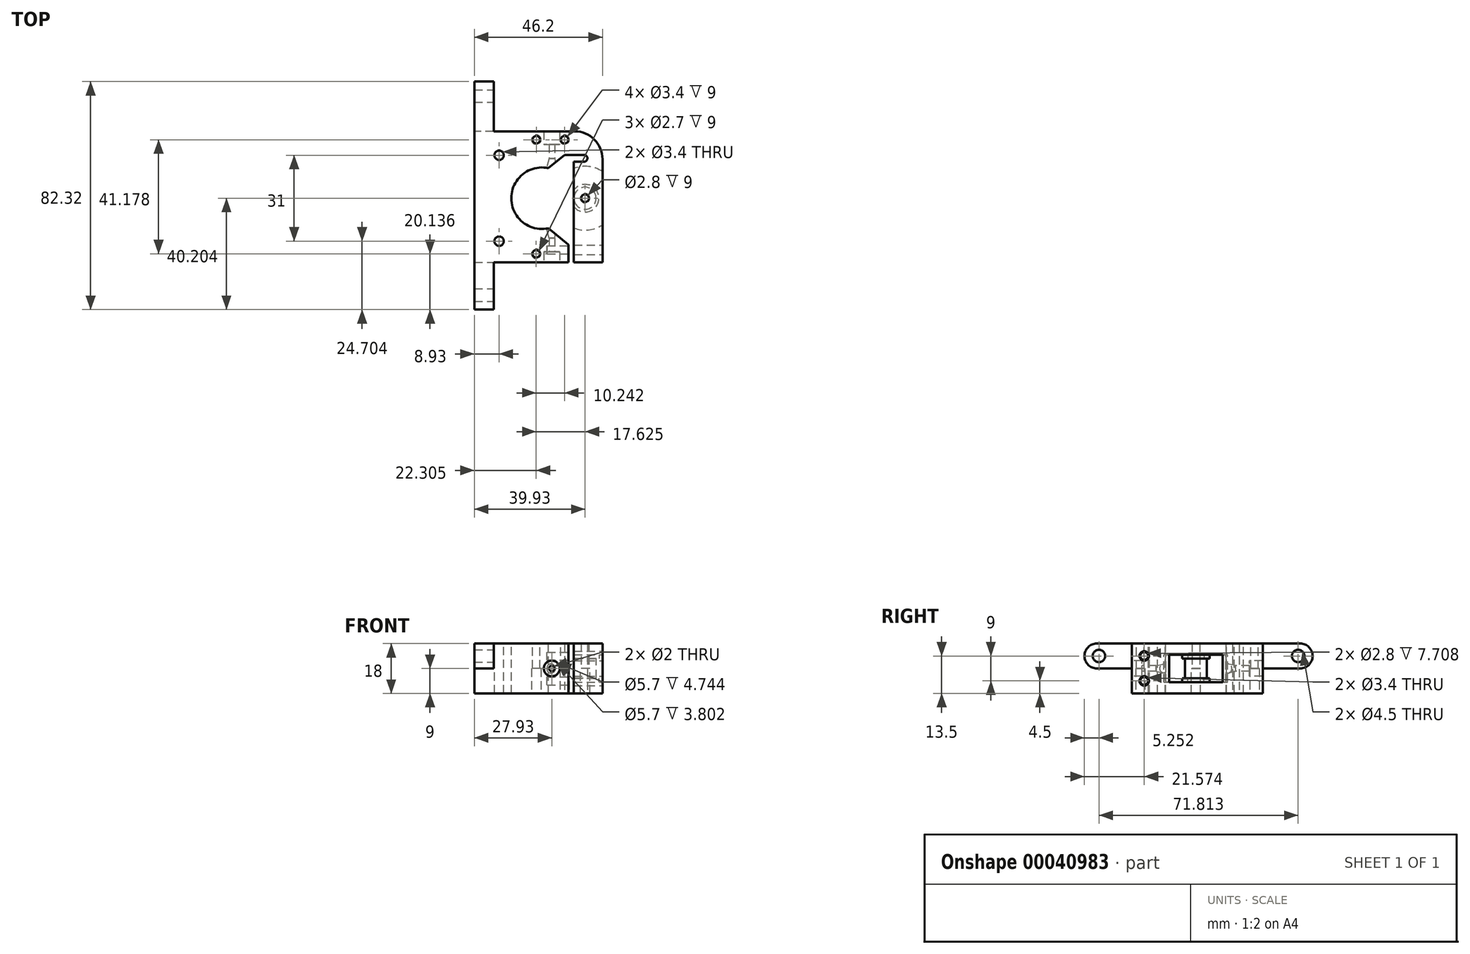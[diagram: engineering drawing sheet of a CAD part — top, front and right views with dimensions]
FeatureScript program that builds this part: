
annotation { "Feature Type Name" : "Feature", "Feature Type Description" : "" }
export const myFeature = defineFeature(function(context is Context, id is Id, definition is map)
    precondition{}
    {
        {
            var Q0;
            Q0=qCreatedBy(makeId("Top.planeOp"),FACE);
            var sketch = newSketch(context, id + "F0", { "sketchPlane" : qUnion([Q0])});
            skLineSegment(sketch, "E0", {"start": v(-24.43, 29.94) * mm, "end": v(-24.43, -17.36) * mm});
            skLineSegment(sketch, "E1", {"start": v(-24.43, -17.36) * mm, "end": v(-24.43, -17.36) * mm});
            skLineSegment(sketch, "E2", {"start": v(-24.43, -17.36) * mm, "end": v(-24.43, -17.35) * mm});
            skLineSegment(sketch, "E3", {"start": v(-24.43, -17.35) * mm, "end": v(9.48, -17.35) * mm});
            skLineSegment(sketch, "E4", {"start": v(9.48, -17.35) * mm, "end": v(9.48, 21.46) * mm});
            skLineSegment(sketch, "E5", {"start": v(9.48, 21.46) * mm, "end": v(15.14, 21.46) * mm});
            skLineSegment(sketch, "E6", {"start": v(15.14, 19) * mm, "end": v(11.48, 19) * mm});
            skLineSegment(sketch, "E7", {"start": v(11.48, 19) * mm, "end": v(11.48, -17.35) * mm});
            skLineSegment(sketch, "E8", {"start": v(11.48, -17.35) * mm, "end": v(21.77, -17.35) * mm});
            skLineSegment(sketch, "E9", {"start": v(21.77, -17.35) * mm, "end": v(21.77, 29.94) * mm});
            skLineSegment(sketch, "E10", {"start": v(21.77, 29.94) * mm, "end": v(-24.43, 29.94) * mm});
            skCircle(sketch, "E11", {"center": v(-2.07, 26.93) * mm, "radius": 1.35 * mm});
            skCircle(sketch, "E12", {"center": v(8.12, 26.93) * mm, "radius": 1.35 * mm});
            skCircle(sketch, "E13", {"center": v(-2.12, -14.24) * mm, "radius": 1.35 * mm});
            skArc(sketch, "E14", {"start": v(15.14, 19) * mm, "mid": v(16.36, 20.23) * mm, "end": v(15.14, 21.46) * mm});
            skCircle(sketch, "E15", {"center": v(-2.07, 26.93) * mm, "radius": 1.7 * mm});
            skCircle(sketch, "E16", {"center": v(8.12, 26.93) * mm, "radius": 1.7 * mm});
            skCircle(sketch, "E17", {"center": v(-2.12, -14.24) * mm, "radius": 1.7 * mm});
            skSolve(sketch);
        }
        {
            var Q0;
            Q0=makeQuery(id+"F0.imprint","IMPRINT",FACE,{"disambiguationData":[TD([[makeQuery(id+"F0.imprint","IMPRINT",EDGE,{"derivedFrom":sQuery(id+"F0.wireOp",EDGE,"E0")}),1.0]])]});
            extrude(context, id + "F1", {"entities" : qUnion([Q0]), "depth" : 9 * mm});
        }
        {
            var Q0;
            Q0=makeQuery(id+"F1.opExtrude","CAP_FACE",FACE,{"disambiguationData":[OSD([sQuery(id+"F0.wireOp",EDGE,"E0"),sQuery(id+"F0.wireOp",EDGE,"E1"),sQuery(id+"F0.wireOp",EDGE,"E2"),sQuery(id+"F0.wireOp",EDGE,"E3"),sQuery(id+"F0.wireOp",EDGE,"E4"),sQuery(id+"F0.wireOp",EDGE,"E5"),sQuery(id+"F0.wireOp",EDGE,"E6"),sQuery(id+"F0.wireOp",EDGE,"E7"),sQuery(id+"F0.wireOp",EDGE,"E8"),sQuery(id+"F0.wireOp",EDGE,"E9"),sQuery(id+"F0.wireOp",EDGE,"E10"),sQuery(id+"F0.wireOp",EDGE,"604cad85-587a-4b7d-8070-06f4cba85480"),sQuery(id+"F0.wireOp",EDGE,"6e5e38c1-5bff-4efe-a8c5-b84022f0a049"),sQuery(id+"F0.wireOp",EDGE,"b8144507-9dd7-4af4-87a3-7b649dd00ae6"),sQuery(id+"F0.wireOp",EDGE,"b9c2cb7c-5e58-4995-888e-a78f0403fbb5"),sQuery(id+"F0.wireOp",EDGE,"885990ab-7576-4c23-8475-595d2769e284"),sQuery(id+"F0.wireOp",EDGE,"E11"),sQuery(id+"F0.wireOp",EDGE,"E12"),sQuery(id+"F0.wireOp",EDGE,"E13"),sQuery(id+"F0.wireOp",EDGE,"E14")])],"isStart":false});
            var sketch = newSketch(context, id + "F2", { "sketchPlane" : qUnion([Q0])});
            skCircle(sketch, "E18", {"center": v(0, 5.82) * mm, "radius": 11.1 * mm});
            skCircle(sketch, "E19", {"center": v(-15.5, 21.32) * mm, "radius": 1.7 * mm});
            skCircle(sketch, "E20", {"center": v(-15.5, -9.68) * mm, "radius": 1.7 * mm});
            skSolve(sketch);
        }
        {
            var Q0;
            Q0=qSketchRegion(id+"F2",true);
            extrude(context, id + "F3", {"entities" : qUnion([Q0]), "operationType" : NewBodyOperationType.REMOVE, "endBound" : BoundingType.THROUGH_ALL, "oppositeDirection" : true, "depth" : 25 * mm});
        }
        {
            var Q0;
            Q0=makeQuery(id+"F1.opExtrude","CAP_FACE",FACE,{"disambiguationData":[OSD([sQuery(id+"F0.wireOp",EDGE,"E0"),sQuery(id+"F0.wireOp",EDGE,"E1"),sQuery(id+"F0.wireOp",EDGE,"E2"),sQuery(id+"F0.wireOp",EDGE,"E3"),sQuery(id+"F0.wireOp",EDGE,"E4"),sQuery(id+"F0.wireOp",EDGE,"E5"),sQuery(id+"F0.wireOp",EDGE,"E6"),sQuery(id+"F0.wireOp",EDGE,"E7"),sQuery(id+"F0.wireOp",EDGE,"E8"),sQuery(id+"F0.wireOp",EDGE,"E9"),sQuery(id+"F0.wireOp",EDGE,"E10"),sQuery(id+"F0.wireOp",EDGE,"604cad85-587a-4b7d-8070-06f4cba85480"),sQuery(id+"F0.wireOp",EDGE,"6e5e38c1-5bff-4efe-a8c5-b84022f0a049"),sQuery(id+"F0.wireOp",EDGE,"E11"),sQuery(id+"F0.wireOp",EDGE,"E12"),sQuery(id+"F0.wireOp",EDGE,"E13"),sQuery(id+"F0.wireOp",EDGE,"E14")])],"isStart":false});
            var sketch = newSketch(context, id + "F4", { "sketchPlane" : qUnion([Q0])});
            skCircle(sketch, "E21", {"center": v(15.5, 5.82) * mm, "radius": 11.5 * mm});
            skCircle(sketch, "E22", {"center": v(15.5, 5.82) * mm, "radius": 5 * mm});
            skCircle(sketch, "E23", {"center": v(15.5, 5.82) * mm, "radius": 4 * mm});
            skLineSegment(sketch, "E24", {"start": v(0, 5.82) * mm, "end": v(31, 5.82) * mm, "construction": true});
            skCircle(sketch, "E25", {"center": v(15.5, 5.82) * mm, "radius": 1.4 * mm});
            skCircle(sketch, "E26", {"center": v(15.5, 5.82) * mm, "radius": 1.7 * mm});
            skSolve(sketch);
        }
        {
            var Q0;
            Q0=makeQuery(id+"F4.imprint","IMPRINT",FACE,{"disambiguationData":[TD([[makeQuery(id+"F4.imprint","IMPRINT",EDGE,{"derivedFrom":sQuery(id+"F4.wireOp",EDGE,"E22")}),-1.0]])]});
            extrude(context, id + "F5", {"entities" : qUnion([Q0]), "operationType" : NewBodyOperationType.REMOVE, "oppositeDirection" : true, "depth" : 5 * mm});
        }
        {
            var Q0;
            Q0=makeQuery(id+"F4.imprint","IMPRINT",FACE,{"disambiguationData":[TD([[makeQuery(id+"F4.imprint","IMPRINT",EDGE,{"derivedFrom":sQuery(id+"F4.wireOp",EDGE,"E22")}),1.0]])]});
            var Q1;
            Q1=makeQuery(id+"F4.imprint","IMPRINT",FACE,{"disambiguationData":[TD([[makeQuery(id+"F4.imprint","IMPRINT",EDGE,{"derivedFrom":sQuery(id+"F4.wireOp",EDGE,"E23")}),-1.0]])]});
            extrude(context, id + "F6", {"entities" : qUnion([Q0, Q1]), "operationType" : NewBodyOperationType.REMOVE, "oppositeDirection" : true, "depth" : 3.5 * mm});
        }
        {
            var Q0;
            {var subQ0=sQuery(id+"F0.wireOp",EDGE,"E0");var subQ1=sQuery(id+"F0.wireOp",EDGE,"E1");var subQ2=sQuery(id+"F0.wireOp",EDGE,"E2");var subQ3=sQuery(id+"F0.wireOp",EDGE,"E3");var subQ4=sQuery(id+"F0.wireOp",EDGE,"E4");var subQ5=sQuery(id+"F0.wireOp",EDGE,"E5");var subQ6=sQuery(id+"F0.wireOp",EDGE,"E6");var subQ7=sQuery(id+"F0.wireOp",EDGE,"E7");var subQ8=sQuery(id+"F0.wireOp",EDGE,"E9");var subQ9=sQuery(id+"F0.wireOp",EDGE,"E10");var subQ10=sQuery(id+"F0.wireOp",EDGE,"604cad85-587a-4b7d-8070-06f4cba85480");var subQ11=sQuery(id+"F0.wireOp",EDGE,"6e5e38c1-5bff-4efe-a8c5-b84022f0a049");var subQ12=sQuery(id+"F0.wireOp",EDGE,"E11");var subQ13=sQuery(id+"F0.wireOp",EDGE,"E12");var subQ14=sQuery(id+"F0.wireOp",EDGE,"E13");var subQ15=sQuery(id+"F0.wireOp",EDGE,"E14");Q0=makeQuery(id+"F5.boolean.opBoolean","SPLIT",FACE,{"disambiguationData":[TD([makeQuery(id+"F1.opExtrude","SWEPT_FACE",FACE,{"disambiguationData":[OSD([subQ0])]})])],"derivedFrom":makeQuery(id+"F1.opExtrude","CAP_FACE",FACE,{"disambiguationData":[OSD([subQ0,subQ1,subQ2,subQ3,subQ4,subQ5,subQ6,subQ7,sQuery(id+"F0.wireOp",EDGE,"E8"),subQ8,subQ9,subQ10,subQ11,subQ12,subQ13,subQ14,subQ15])],"isStart":false})});}
            var sketch = newSketch(context, id + "F7", { "sketchPlane" : qUnion([Q0])});
            skLineSegment(sketch, "E27", {"start": v(0.65, 30.2) * mm, "end": v(0.65, 25.2) * mm});
            skLineSegment(sketch, "E28", {"start": v(0.65, 25.2) * mm, "end": v(2.5, 25.2) * mm});
            skLineSegment(sketch, "E29", {"start": v(2.5, 25.2) * mm, "end": v(2.5, 20.21) * mm});
            skLineSegment(sketch, "E30", {"start": v(2.5, 20.21) * mm, "end": v(1.31, 15.18) * mm});
            skLineSegment(sketch, "E31", {"start": v(1.31, 15.18) * mm, "end": v(3.5, 15.18) * mm});
            skLineSegment(sketch, "E32", {"start": v(3.5, 15.18) * mm, "end": v(3.5, 30.2) * mm});
            skLineSegment(sketch, "E33", {"start": v(3.5, 30.2) * mm, "end": v(0.65, 30.2) * mm});
            skLineSegment(sketch, "E34", {"start": v(0, 5.82) * mm, "end": v(31.4, 5.82) * mm, "construction": true});
            skLineSegment(sketch, "E35.0.MirrorCS", {"start": v(0.65, -13.54) * mm, "end": v(2.5, -13.54) * mm});
            skLineSegment(sketch, "E35.1.MirrorCS", {"start": v(3.5, -3.53) * mm, "end": v(3.5, -18.54) * mm});
            skLineSegment(sketch, "E35.2.MirrorCS", {"start": v(0.65, -18.54) * mm, "end": v(0.65, -13.54) * mm});
            skLineSegment(sketch, "E35.3.MirrorCS", {"start": v(1.31, -3.53) * mm, "end": v(3.5, -3.53) * mm});
            skLineSegment(sketch, "E35.4.MirrorCS", {"start": v(2.5, -8.56) * mm, "end": v(1.31, -3.53) * mm});
            skLineSegment(sketch, "E35.5.MirrorCS", {"start": v(2.5, -13.54) * mm, "end": v(2.5, -8.56) * mm});
            skLineSegment(sketch, "E35.6.MirrorCS", {"start": v(3.5, -18.54) * mm, "end": v(0.65, -18.54) * mm});
            skSolve(sketch);
        }
        {
            var Q0;
            Q0=qSketchRegion(id+"F7",true);
            var Q1;
            Q1=sQuery(id+"F7.wireOp",EDGE,"E32");
            revolve(context, id + "F8", {"entities" : qUnion([Q0]), "axis" : qUnion([Q1]), "revolveType" : RevolveType.FULL});
        }
        {
            var Q0;
            Q0=makeQuery(id+"F8.opRevolve","SWEPT_BODY",BODY,{"disambiguationData":[OSD([sQuery(id+"F7.wireOp",EDGE,"E27"),sQuery(id+"F7.wireOp",EDGE,"E28"),sQuery(id+"F7.wireOp",EDGE,"E29"),sQuery(id+"F7.wireOp",EDGE,"E30"),sQuery(id+"F7.wireOp",EDGE,"E31"),sQuery(id+"F7.wireOp",EDGE,"E32"),sQuery(id+"F7.wireOp",EDGE,"E33")])]});
            var Q1;
            Q1=makeQuery(id+"F1.opExtrude","SWEPT_BODY",BODY,{"disambiguationData":[OSD([sQuery(id+"F0.wireOp",EDGE,"E0"),sQuery(id+"F0.wireOp",EDGE,"E1"),sQuery(id+"F0.wireOp",EDGE,"E2"),sQuery(id+"F0.wireOp",EDGE,"E3"),sQuery(id+"F0.wireOp",EDGE,"E4"),sQuery(id+"F0.wireOp",EDGE,"E5"),sQuery(id+"F0.wireOp",EDGE,"E6"),sQuery(id+"F0.wireOp",EDGE,"E7"),sQuery(id+"F0.wireOp",EDGE,"E8"),sQuery(id+"F0.wireOp",EDGE,"E9"),sQuery(id+"F0.wireOp",EDGE,"E10"),sQuery(id+"F0.wireOp",EDGE,"604cad85-587a-4b7d-8070-06f4cba85480"),sQuery(id+"F0.wireOp",EDGE,"6e5e38c1-5bff-4efe-a8c5-b84022f0a049"),sQuery(id+"F0.wireOp",EDGE,"E11"),sQuery(id+"F0.wireOp",EDGE,"E12"),sQuery(id+"F0.wireOp",EDGE,"E13"),sQuery(id+"F0.wireOp",EDGE,"E14")])]});
            booleanBodies(context, id + "F9", {"operationType" : BooleanOperationType.SUBTRACTION, "tools" : qUnion([Q0]), "targets" : qUnion([Q1]), "keepTools" : true});
        }
        {
            var Q0;
            Q0=makeQuery(id+"F8.opRevolve","SWEPT_BODY",BODY,{"disambiguationData":[OSD([sQuery(id+"F7.wireOp",EDGE,"E35.0.MirrorCS"),sQuery(id+"F7.wireOp",EDGE,"E35.1.MirrorCS"),sQuery(id+"F7.wireOp",EDGE,"E35.2.MirrorCS"),sQuery(id+"F7.wireOp",EDGE,"E35.3.MirrorCS"),sQuery(id+"F7.wireOp",EDGE,"E35.4.MirrorCS"),sQuery(id+"F7.wireOp",EDGE,"E35.5.MirrorCS"),sQuery(id+"F7.wireOp",EDGE,"E35.6.MirrorCS")])]});
            var Q1;
            Q1=makeQuery(id+"F1.opExtrude","SWEPT_BODY",BODY,{"disambiguationData":[OSD([sQuery(id+"F0.wireOp",EDGE,"E0"),sQuery(id+"F0.wireOp",EDGE,"E1"),sQuery(id+"F0.wireOp",EDGE,"E2"),sQuery(id+"F0.wireOp",EDGE,"E3"),sQuery(id+"F0.wireOp",EDGE,"E4"),sQuery(id+"F0.wireOp",EDGE,"E5"),sQuery(id+"F0.wireOp",EDGE,"E6"),sQuery(id+"F0.wireOp",EDGE,"E7"),sQuery(id+"F0.wireOp",EDGE,"E8"),sQuery(id+"F0.wireOp",EDGE,"E9"),sQuery(id+"F0.wireOp",EDGE,"E10"),sQuery(id+"F0.wireOp",EDGE,"604cad85-587a-4b7d-8070-06f4cba85480"),sQuery(id+"F0.wireOp",EDGE,"6e5e38c1-5bff-4efe-a8c5-b84022f0a049"),sQuery(id+"F0.wireOp",EDGE,"E11"),sQuery(id+"F0.wireOp",EDGE,"E12"),sQuery(id+"F0.wireOp",EDGE,"E13"),sQuery(id+"F0.wireOp",EDGE,"E14")])]});
            booleanBodies(context, id + "F10", {"operationType" : BooleanOperationType.SUBTRACTION, "tools" : qUnion([Q0]), "targets" : qUnion([Q1]), "keepTools" : true});
        }
        {
            var Q0;
            Q0=makeQuery(id+"F1.opExtrude","SWEPT_EDGE",EDGE,{"disambiguationData":[OSD([sQuery(id+"F0.wireOp",EDGE,"E9"),sQuery(id+"F0.wireOp",EDGE,"E10")])]});
            fillet(context, id + "F11", {"entities" : qUnion([Q0]), "radius" : 10 * mm, "tangentPropagation" : true, "allowEdgeOverflow" : false});
        }
        {
            var Q0;
            Q0=qSketchRegion(id+"F0",true);
            var Q1;
            Q1=makeQuery(id+"F0.imprint","IMPRINT",FACE,{"disambiguationData":[TD([[makeQuery(id+"F0.imprint","IMPRINT",EDGE,{"derivedFrom":sQuery(id+"F0.wireOp",EDGE,"E12")}),-1.0]])]});
            var Q2;
            Q2=makeQuery(id+"F0.imprint","IMPRINT",FACE,{"disambiguationData":[TD([[makeQuery(id+"F0.imprint","IMPRINT",EDGE,{"derivedFrom":sQuery(id+"F0.wireOp",EDGE,"E11")}),-1.0]])]});
            var Q3;
            Q3=makeQuery(id+"F0.imprint","IMPRINT",FACE,{"disambiguationData":[TD([[makeQuery(id+"F0.imprint","IMPRINT",EDGE,{"derivedFrom":sQuery(id+"F0.wireOp",EDGE,"E13")}),-1.0]])]});
            extrude(context, id + "F12", {"entities" : qUnion([Q0, Q1, Q2, Q3]), "oppositeDirection" : true, "depth" : 9 * mm});
        }
        {
            var Q0;
            Q0=makeQuery(id+"F12.opExtrude","SWEPT_BODY",BODY,{"disambiguationData":[OSD([sQuery(id+"F0.wireOp",EDGE,"E0"),sQuery(id+"F0.wireOp",EDGE,"E3"),sQuery(id+"F0.wireOp",EDGE,"E4"),sQuery(id+"F0.wireOp",EDGE,"E5"),sQuery(id+"F0.wireOp",EDGE,"E6"),sQuery(id+"F0.wireOp",EDGE,"E7"),sQuery(id+"F0.wireOp",EDGE,"E8"),sQuery(id+"F0.wireOp",EDGE,"E9"),sQuery(id+"F0.wireOp",EDGE,"E10"),sQuery(id+"F0.wireOp",EDGE,"E11"),sQuery(id+"F0.wireOp",EDGE,"E12"),sQuery(id+"F0.wireOp",EDGE,"E13"),sQuery(id+"F0.wireOp",EDGE,"E14")])]});
            transform(context, id + "F13", {"entities" : qUnion([Q0]), "transformType" : TransformType.TRANSLATION_3D, "dx" : 0 * mm, "dy" : 0 * mm, "dz" : 18 * mm, "makeCopy" : false});
        }
        {
            var Q0;
            Q0=makeQuery(id+"F12.opExtrude","SWEPT_EDGE",EDGE,{"disambiguationData":[OSD([sQuery(id+"F0.wireOp",EDGE,"E9"),sQuery(id+"F0.wireOp",EDGE,"E10")])]});
            fillet(context, id + "F14", {"entities" : qUnion([Q0]), "radius" : 10 * mm, "tangentPropagation" : true, "allowEdgeOverflow" : false});
        }
        {
            var Q0;
            Q0=qSketchRegion(id+"F2",true);
            extrude(context, id + "F15", {"entities" : qUnion([Q0]), "operationType" : NewBodyOperationType.REMOVE, "endBound" : BoundingType.THROUGH_ALL, "depth" : 25 * mm});
        }
        {
            var Q0;
            {var subQ3=sQuery(id+"F4.wireOp",EDGE,"E21");var subQ7=makeQuery(id+"F1.opExtrude","CAP_EDGE",EDGE,{"disambiguationData":[OSD([sQuery(id+"F0.wireOp",EDGE,"E9")])],"isStart":false});var subQ9=makeQuery(id+"F4.imprint","INTERSECT",VERTEX,{"disambiguationData":[OD(0.0)],"derivedFrom":[subQ7,subQ3]});Q0=makeQuery(id+"F4.imprint","IMPRINT",FACE,{"disambiguationData":[TD([[makeQuery(id+"F4.imprint","IMPRINT",EDGE,{"disambiguationData":[TD([[subQ9,-1.0]])],"derivedFrom":subQ3}),1.0]])]});}
            extrude(context, id + "F16", {"entities" : qUnion([Q0]), "operationType" : NewBodyOperationType.REMOVE, "depth" : 5 * mm});
        }
        {
            var Q0;
            Q0=makeQuery(id+"F4.imprint","IMPRINT",FACE,{"disambiguationData":[TD([[makeQuery(id+"F4.imprint","IMPRINT",EDGE,{"derivedFrom":sQuery(id+"F4.wireOp",EDGE,"E23")}),-1.0]])]});
            extrude(context, id + "F17", {"entities" : qUnion([Q0]), "operationType" : NewBodyOperationType.REMOVE, "depth" : 3.5 * mm});
        }
        {
            var Q0;
            Q0=makeQuery(id+"F8.opRevolve","SWEPT_BODY",BODY,{"disambiguationData":[OSD([sQuery(id+"F7.wireOp",EDGE,"E27"),sQuery(id+"F7.wireOp",EDGE,"E28"),sQuery(id+"F7.wireOp",EDGE,"E29"),sQuery(id+"F7.wireOp",EDGE,"E30"),sQuery(id+"F7.wireOp",EDGE,"E31"),sQuery(id+"F7.wireOp",EDGE,"E32"),sQuery(id+"F7.wireOp",EDGE,"E33")])]});
            var Q1;
            Q1=makeQuery(id+"F12.opExtrude","SWEPT_BODY",BODY,{"disambiguationData":[OSD([sQuery(id+"F0.wireOp",EDGE,"E0"),sQuery(id+"F0.wireOp",EDGE,"E3"),sQuery(id+"F0.wireOp",EDGE,"E4"),sQuery(id+"F0.wireOp",EDGE,"E5"),sQuery(id+"F0.wireOp",EDGE,"E6"),sQuery(id+"F0.wireOp",EDGE,"E7"),sQuery(id+"F0.wireOp",EDGE,"E8"),sQuery(id+"F0.wireOp",EDGE,"E9"),sQuery(id+"F0.wireOp",EDGE,"E10"),sQuery(id+"F0.wireOp",EDGE,"E11"),sQuery(id+"F0.wireOp",EDGE,"E12"),sQuery(id+"F0.wireOp",EDGE,"E13"),sQuery(id+"F0.wireOp",EDGE,"E14")])]});
            booleanBodies(context, id + "F18", {"operationType" : BooleanOperationType.SUBTRACTION, "tools" : qUnion([Q0]), "targets" : qUnion([Q1])});
        }
        {
            var Q0;
            Q0=makeQuery(id+"F8.opRevolve","SWEPT_BODY",BODY,{"disambiguationData":[OSD([sQuery(id+"F7.wireOp",EDGE,"E35.0.MirrorCS"),sQuery(id+"F7.wireOp",EDGE,"E35.1.MirrorCS"),sQuery(id+"F7.wireOp",EDGE,"E35.2.MirrorCS"),sQuery(id+"F7.wireOp",EDGE,"E35.3.MirrorCS"),sQuery(id+"F7.wireOp",EDGE,"E35.4.MirrorCS"),sQuery(id+"F7.wireOp",EDGE,"E35.5.MirrorCS"),sQuery(id+"F7.wireOp",EDGE,"E35.6.MirrorCS")])]});
            var Q1;
            Q1=makeQuery(id+"F12.opExtrude","SWEPT_BODY",BODY,{"disambiguationData":[OSD([sQuery(id+"F0.wireOp",EDGE,"E0"),sQuery(id+"F0.wireOp",EDGE,"E3"),sQuery(id+"F0.wireOp",EDGE,"E4"),sQuery(id+"F0.wireOp",EDGE,"E5"),sQuery(id+"F0.wireOp",EDGE,"E6"),sQuery(id+"F0.wireOp",EDGE,"E7"),sQuery(id+"F0.wireOp",EDGE,"E8"),sQuery(id+"F0.wireOp",EDGE,"E9"),sQuery(id+"F0.wireOp",EDGE,"E10"),sQuery(id+"F0.wireOp",EDGE,"E11"),sQuery(id+"F0.wireOp",EDGE,"E12"),sQuery(id+"F0.wireOp",EDGE,"E13"),sQuery(id+"F0.wireOp",EDGE,"E14")])]});
            booleanBodies(context, id + "F19", {"operationType" : BooleanOperationType.SUBTRACTION, "tools" : qUnion([Q0]), "targets" : qUnion([Q1])});
        }
        {
            var Q0;
            Q0=makeQuery(id+"F12.opExtrude","SWEPT_FACE",FACE,{"disambiguationData":[OSD([sQuery(id+"F0.wireOp",EDGE,"E9")])]});
            var sketch = newSketch(context, id + "F20", { "sketchPlane" : qUnion([Q0])});
            skCircle(sketch, "E36", {"center": v(-12.8, 13.5) * mm, "radius": 1.7 * mm});
            skCircle(sketch, "E37", {"center": v(-12.8, 13.5) * mm, "radius": 1.4 * mm});
            skCircle(sketch, "E38", {"center": v(-12.8, 4.5) * mm, "radius": 1.7 * mm});
            skCircle(sketch, "E39", {"center": v(-12.8, 4.5) * mm, "radius": 1.4 * mm});
            skSolve(sketch);
        }
        {
            var Q0;
            Q0=makeQuery(id+"F20.imprint","IMPRINT",FACE,{"disambiguationData":[TD([[makeQuery(id+"F20.imprint","IMPRINT",EDGE,{"derivedFrom":sQuery(id+"F20.wireOp",EDGE,"E37")}),1.0]])]});
            extrude(context, id + "F21", {"entities" : qUnion([Q0]), "operationType" : NewBodyOperationType.REMOVE, "oppositeDirection" : true, "depth" : 20 * mm});
        }
        {
            var Q0;
            Q0=makeQuery(id+"F20.imprint","IMPRINT",FACE,{"disambiguationData":[TD([[makeQuery(id+"F20.imprint","IMPRINT",EDGE,{"derivedFrom":sQuery(id+"F20.wireOp",EDGE,"E36")}),1.0]])]});
            extrude(context, id + "F22", {"entities" : qUnion([Q0]), "operationType" : NewBodyOperationType.REMOVE, "oppositeDirection" : true, "depth" : 11 * mm});
        }
        {
            var Q0;
            Q0=makeQuery(id+"F20.imprint","IMPRINT",FACE,{"disambiguationData":[TD([[makeQuery(id+"F20.imprint","IMPRINT",EDGE,{"derivedFrom":sQuery(id+"F20.wireOp",EDGE,"E39")}),1.0]])]});
            extrude(context, id + "F23", {"entities" : qUnion([Q0]), "operationType" : NewBodyOperationType.REMOVE, "oppositeDirection" : true, "depth" : 20 * mm});
        }
        {
            var Q0;
            Q0=makeQuery(id+"F20.imprint","IMPRINT",FACE,{"disambiguationData":[TD([[makeQuery(id+"F20.imprint","IMPRINT",EDGE,{"derivedFrom":sQuery(id+"F20.wireOp",EDGE,"E38")}),1.0]])]});
            extrude(context, id + "F24", {"entities" : qUnion([Q0]), "operationType" : NewBodyOperationType.REMOVE, "oppositeDirection" : true, "depth" : 11 * mm});
        }
        {
            var Q0;
            Q0=makeQuery(id+"F4.imprint","IMPRINT",FACE,{"disambiguationData":[TD([[makeQuery(id+"F4.imprint","IMPRINT",EDGE,{"derivedFrom":sQuery(id+"F4.wireOp",EDGE,"E25")}),1.0]])]});
            var Q1;
            Q1=makeQuery(id+"F4.imprint","IMPRINT",FACE,{"disambiguationData":[TD([[makeQuery(id+"F4.imprint","IMPRINT",EDGE,{"derivedFrom":sQuery(id+"F4.wireOp",EDGE,"E25")}),-1.0]])]});
            extrude(context, id + "F25", {"entities" : qUnion([Q0, Q1]), "operationType" : NewBodyOperationType.REMOVE, "oppositeDirection" : true, "depth" : 25 * mm});
        }
        {
            var Q0;
            Q0=makeQuery(id+"F4.imprint","IMPRINT",FACE,{"disambiguationData":[TD([[makeQuery(id+"F4.imprint","IMPRINT",EDGE,{"derivedFrom":sQuery(id+"F4.wireOp",EDGE,"E25")}),1.0]])]});
            extrude(context, id + "F26", {"entities" : qUnion([Q0]), "operationType" : NewBodyOperationType.REMOVE, "depth" : 25 * mm});
        }
        {
            var Q0;
            Q0=makeQuery(id+"F12.opExtrude","SWEPT_FACE",FACE,{"disambiguationData":[OSD([sQuery(id+"F0.wireOp",EDGE,"E10")])]});
            var sketch = newSketch(context, id + "F27", { "sketchPlane" : qUnion([Q0])});
            skLineSegment(sketch, "E40.bottom", {"start": v(24.43, 9) * mm, "end": v(17.43, 9) * mm});
            skLineSegment(sketch, "E40.top", {"start": v(24.43, 18) * mm, "end": v(17.43, 18) * mm});
            skLineSegment(sketch, "E40.left", {"start": v(24.43, 9) * mm, "end": v(24.43, 18) * mm});
            skLineSegment(sketch, "E40.right", {"start": v(17.43, 9) * mm, "end": v(17.43, 18) * mm});
            skSolve(sketch);
        }
        {
            var Q0;
            Q0=qSketchRegion(id+"F27",true);
            extrude(context, id + "F28", {"entities" : qUnion([Q0]), "operationType" : NewBodyOperationType.ADD, "depth" : 18 * mm, "hasSecondDirection" : true, "secondDirectionOppositeDirection" : true, "secondDirectionDepth" : 64.31 * mm});
        }
        {
            var Q0;
            {var subQ0=sQuery(id+"F27.wireOp",EDGE,"E40.right");var subQ3=sQuery(id+"F0.wireOp",EDGE,"E3");Q0=makeQuery(id+"F28.boolean.opBoolean","SPLIT",FACE,{"disambiguationData":[TD([makeQuery(id+"F12.opExtrude","SWEPT_FACE",FACE,{"disambiguationData":[OSD([subQ3])]})])],"derivedFrom":makeQuery(id+"F28.opExtrude","SWEPT_FACE",FACE,{"disambiguationData":[OSD([subQ0])]})});}
            var sketch = newSketch(context, id + "F29", { "sketchPlane" : qUnion([Q0])});
            skCircle(sketch, "E41", {"center": v(-29.13, 13.5) * mm, "radius": 2.25 * mm});
            skPoint(sketch, "E42", {"position": v(-34.38, 13.5) * mm});
            skSolve(sketch);
        }
        {
            var Q0;
            {var subQ0=sQuery(id+"F27.wireOp",EDGE,"E40.right");var subQ3=sQuery(id+"F0.wireOp",EDGE,"E10");Q0=makeQuery(id+"F28.boolean.opBoolean","SPLIT",FACE,{"disambiguationData":[TD([makeQuery(id+"F12.opExtrude","SWEPT_FACE",FACE,{"disambiguationData":[OSD([subQ3])]})])],"derivedFrom":makeQuery(id+"F28.opExtrude","SWEPT_FACE",FACE,{"disambiguationData":[OSD([subQ0])]})});}
            var sketch = newSketch(context, id + "F30", { "sketchPlane" : qUnion([Q0])});
            skCircle(sketch, "E43", {"center": v(42.69, 13.5) * mm, "radius": 2.25 * mm});
            skPoint(sketch, "E44", {"position": v(47.94, 13.5) * mm});
            skSolve(sketch);
        }
        {
            var Q0;
            Q0=qSketchRegion(id+"F29",true);
            var Q1;
            Q1=qSketchRegion(id+"F30",true);
            extrude(context, id + "F31", {"entities" : qUnion([Q0, Q1]), "operationType" : NewBodyOperationType.REMOVE, "oppositeDirection" : true, "depth" : 25 * mm});
        }
        {
            var Q0;
            Q0=makeQuery(id+"F28.opExtrude","CAP_EDGE",EDGE,{"disambiguationData":[OSD([sQuery(id+"F27.wireOp",EDGE,"E40.top")])],"isStart":true});
            var Q1;
            Q1=makeQuery(id+"F28.opExtrude","CAP_EDGE",EDGE,{"disambiguationData":[OSD([sQuery(id+"F27.wireOp",EDGE,"E40.bottom")])],"isStart":true});
            var Q2;
            Q2=makeQuery(id+"F28.opExtrude","CAP_EDGE",EDGE,{"disambiguationData":[OSD([sQuery(id+"F27.wireOp",EDGE,"E40.top")])],"isStart":false});
            var Q3;
            Q3=makeQuery(id+"F28.opExtrude","CAP_EDGE",EDGE,{"disambiguationData":[OSD([sQuery(id+"F27.wireOp",EDGE,"E40.bottom")])],"isStart":false});
            fillet(context, id + "F32", {"entities" : qUnion([Q0, Q1, Q2, Q3]), "radius" : 4.5 * mm, "tangentPropagation" : true, "allowEdgeOverflow" : false});
        }
        {
            var Q0;
            Q0=makeQuery(id+"F3.boolean.opBoolean","INTERSECT",EDGE,{"disambiguationData":[OD(0.0)],"derivedFrom":[makeQuery(id+"F1.opExtrude","SWEPT_FACE",FACE,{"disambiguationData":[OSD([sQuery(id+"F0.wireOp",EDGE,"E4")])]}),makeQuery(id+"F3.opExtrude","SWEPT_FACE",FACE,{"disambiguationData":[OSD([sQuery(id+"F2.wireOp",EDGE,"E18")])]})]});
            var Q1;
            Q1=makeQuery(id+"F3.boolean.opBoolean","INTERSECT",EDGE,{"disambiguationData":[OD(1.0)],"derivedFrom":[makeQuery(id+"F1.opExtrude","SWEPT_FACE",FACE,{"disambiguationData":[OSD([sQuery(id+"F0.wireOp",EDGE,"E4")])]}),makeQuery(id+"F3.opExtrude","SWEPT_FACE",FACE,{"disambiguationData":[OSD([sQuery(id+"F2.wireOp",EDGE,"E18")])]})]});
            var Q2;
            Q2=makeQuery(id+"F15.boolean.opBoolean","INTERSECT",EDGE,{"disambiguationData":[OD(1.0)],"derivedFrom":[makeQuery(id+"F12.opExtrude","SWEPT_FACE",FACE,{"disambiguationData":[OSD([sQuery(id+"F0.wireOp",EDGE,"E4")])]}),makeQuery(id+"F15.opExtrude","SWEPT_FACE",FACE,{"disambiguationData":[OSD([sQuery(id+"F2.wireOp",EDGE,"E18")])]})]});
            var Q3;
            Q3=makeQuery(id+"F15.boolean.opBoolean","INTERSECT",EDGE,{"disambiguationData":[OD(0.0)],"derivedFrom":[makeQuery(id+"F12.opExtrude","SWEPT_FACE",FACE,{"disambiguationData":[OSD([sQuery(id+"F0.wireOp",EDGE,"E4")])]}),makeQuery(id+"F15.opExtrude","SWEPT_FACE",FACE,{"disambiguationData":[OSD([sQuery(id+"F2.wireOp",EDGE,"E18")])]})]});
            chamfer(context, id + "F33", {"entities" : qUnion([Q0, Q1, Q2, Q3]), "width" : 6 * mm, "tangentPropagation" : true});
        }
    });
